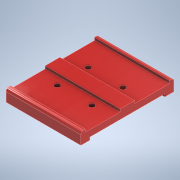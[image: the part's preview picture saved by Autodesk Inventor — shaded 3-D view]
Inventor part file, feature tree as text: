
AUTODESK INVENTOR PART (.ipt)
format: ipt  version: 2021 (Build 250183000, 183)  size: 160,768 bytes
history: native  units: in
note: dims shown in document units (in); Inventor stores cm internally (conversion verified against a paired STEP export)
features: extrude x2, sketch x2
ambient origin geometry x8: Origin, YZ Plane, XZ Plane, XY Plane, X Axis, Y Axis, Z Axis, Center Point
bodies: Solid1 (feature_tree)
feature tree (4):
  extrude  "Extrusion1"  Depth=0.3937in
  extrude  "Extrusion2"  Depth=1.6929in
  sketch  "Sketch1"  dims[d10=0.3937in d11=0.3937in]
  sketch  "Sketch2"  dims[d13=0.1969in d15=1.6929in d16=2.3228in d17=4.0157in d18=0.5118in d19=0.1181in d20=0.1181in d21=3.2283in d22=0.0in d23=1.3386in d24=0.8661in d25=0.2362in d26=1.3386in d27=0.8661in d28=1.3386in d29=0.8661in d30=1.3386in d31=0.8661in d32=0.2362in d33=0.2362in d34=0.2362in d35=2.4409in d36=0.0in]
